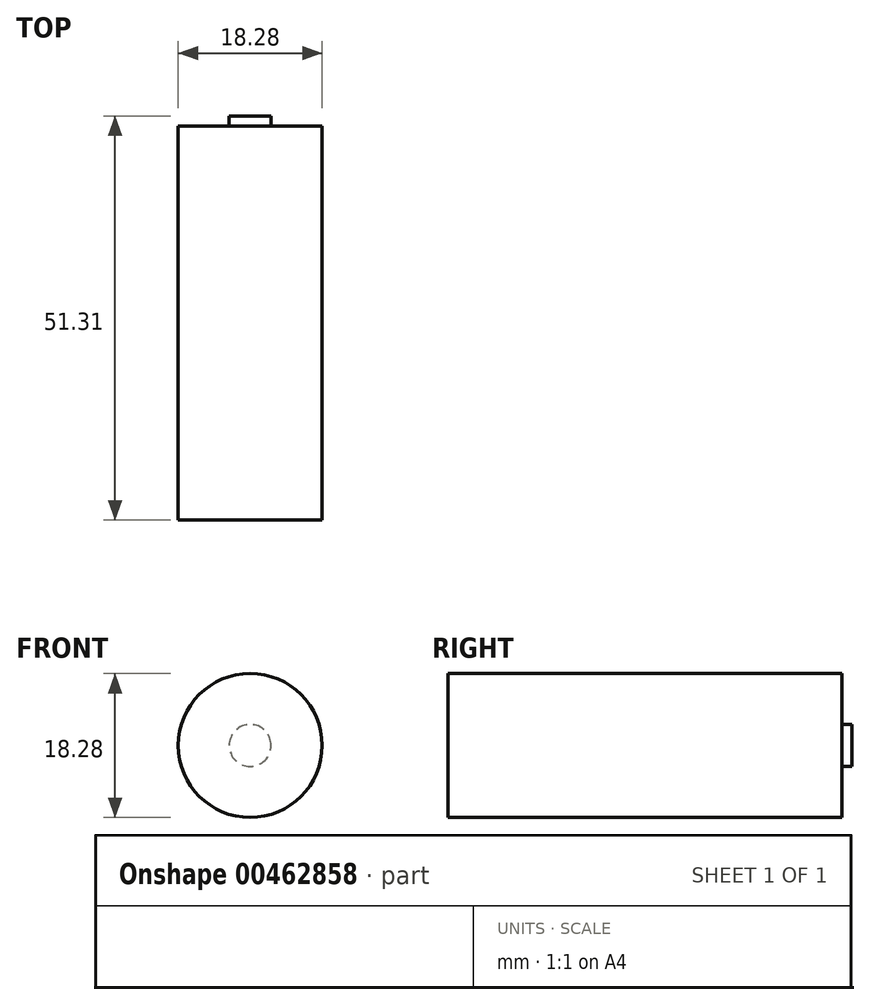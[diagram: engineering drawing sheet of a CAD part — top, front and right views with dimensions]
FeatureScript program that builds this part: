
annotation { "Feature Type Name" : "Feature", "Feature Type Description" : "" }
export const myFeature = defineFeature(function(context is Context, id is Id, definition is map)
    precondition{}
    {
        {
            var Q0;
            Q0=qCreatedBy(makeId("Front.planeOp"),FACE);
            var sketch = newSketch(context, id + "F0", { "sketchPlane" : qUnion([Q0])});
            skCircle(sketch, "E0", {"center": v(0, 0) * mm, "radius": 9.14 * mm});
            skSolve(sketch);
        }
        {
            var Q0;
            Q0 = qSketchRegion(id + "F0", true);
            extrude(context, id + "F1", {"entities" : qUnion([Q0]), "depth" : 25.02 * mm, "offsetDistance" : 25.4 * mm, "hasSecondDirection" : true, "secondDirectionOppositeDirection" : true, "secondDirectionDepth" : 25.02 * mm});
        }
        {
            var Q0;
            Q0=makeQuery(id+"F1.opExtrude","CAP_FACE",FACE,{"disambiguationData":[OSD([sQuery(id+"F0.wireOp",EDGE,"E0")])],"isStart":true});
            var sketch = newSketch(context, id + "F2", { "sketchPlane" : qUnion([Q0])});
            skCircle(sketch, "E1", {"center": v(0, 0) * mm, "radius": 2.67 * mm});
            skSolve(sketch);
        }
        {
            var Q0;
            Q0 = qSketchRegion(id + "F2", true);
            extrude(context, id + "F3", {"entities" : qUnion([Q0]), "operationType" : NewBodyOperationType.ADD, "depth" : 1.27 * mm, "offsetDistance" : 25.4 * mm});
        }
    });
